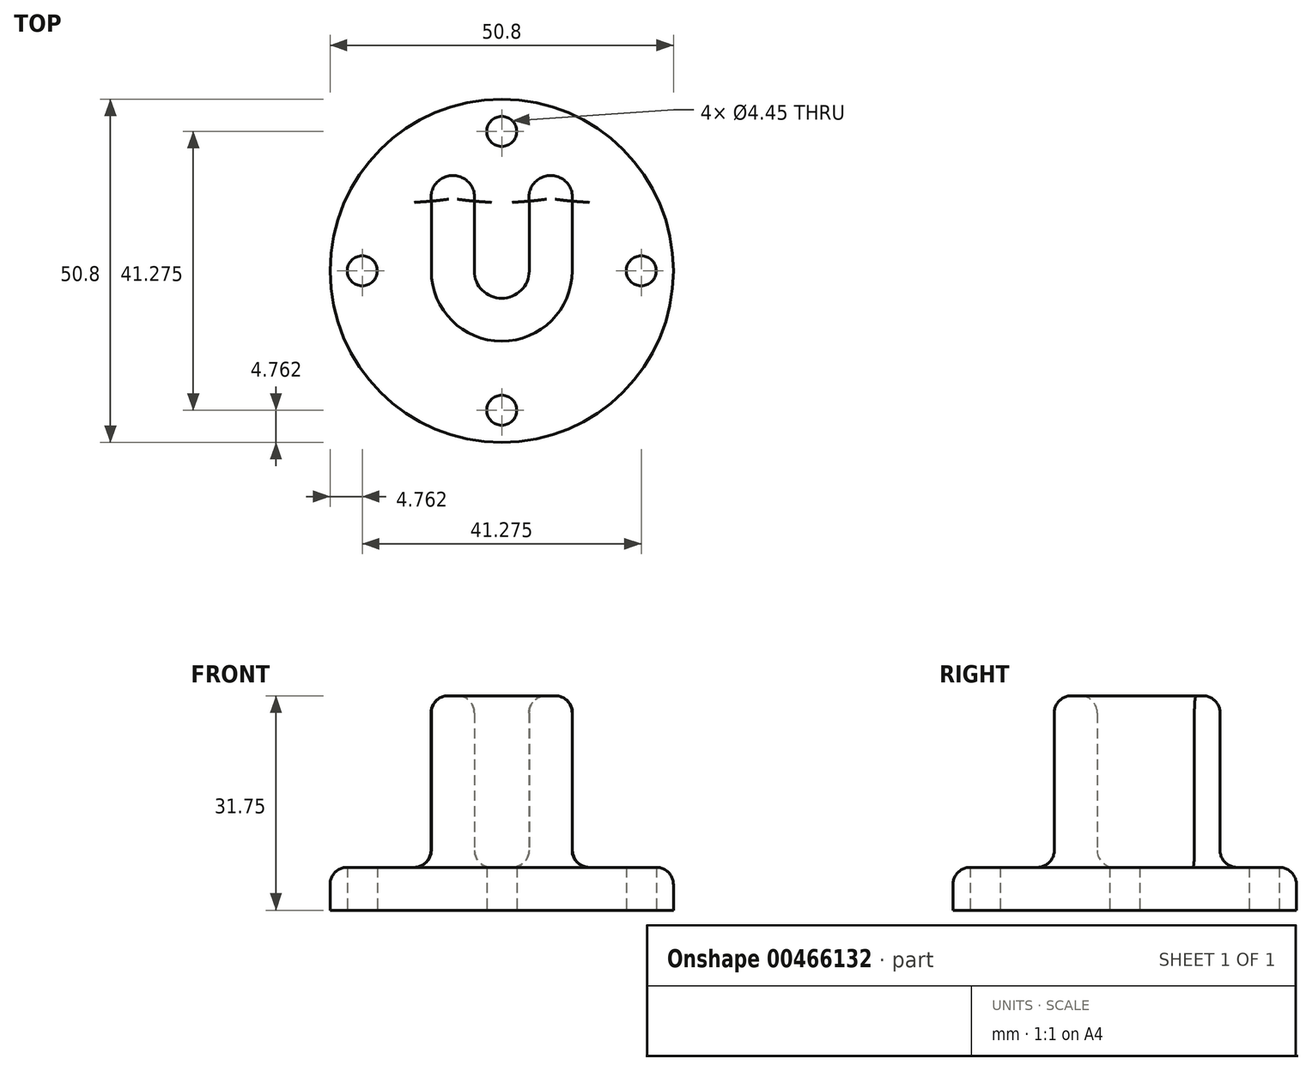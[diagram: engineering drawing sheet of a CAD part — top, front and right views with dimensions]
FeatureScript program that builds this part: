
annotation { "Feature Type Name" : "Feature", "Feature Type Description" : "" }
export const myFeature = defineFeature(function(context is Context, id is Id, definition is map)
    precondition{}
    {
        {
            var Q0;
            Q0=qCreatedBy(makeId("Top.planeOp"),FACE);
            var sketch = newSketch(context, id + "F0", { "sketchPlane" : qUnion([Q0])});
            skCircle(sketch, "E0", {"center": v(0, 0) * mm, "radius": 25.4 * mm});
            skLineSegment(sketch, "E1", {"start": v(0, 41.42) * mm, "end": v(0, -53.18) * mm, "construction": true});
            skLineSegment(sketch, "E2", {"start": v(45.55, 0) * mm, "end": v(-36.4, 0) * mm, "construction": true});
            skCircle(sketch, "E3", {"center": v(0, 0) * mm, "radius": 20.64 * mm, "construction": true});
            skCircle(sketch, "E4", {"center": v(0, 20.64) * mm, "radius": 2.22 * mm});
            skCircle(sketch, "E5.1.0", {"center": v(20.64, 0) * mm, "radius": 2.22 * mm});
            skCircle(sketch, "E5.2.0", {"center": v(0, -20.64) * mm, "radius": 2.22 * mm});
            skCircle(sketch, "E5.3.0", {"center": v(-20.64, 0) * mm, "radius": 2.22 * mm});
            skLineSegment(sketch, "E5.anchor1", {"start": v(0, 0) * mm, "end": v(0, 20.64) * mm, "construction": true});
            skLineSegment(sketch, "E5.anchor2", {"start": v(0, 0) * mm, "end": v(-20.64, 0) * mm, "construction": true});
            skArc(sketch, "E6", {"start": v(-4.06, 0) * mm, "mid": v(0, -4.06) * mm, "end": v(4.06, 0) * mm});
            skArc(sketch, "E7.0", {"start": v(1.4, 10.32) * mm, "mid": v(0.7, 10.4) * mm, "end": v(0, 10.41) * mm});
            skLineSegment(sketch, "E8", {"start": v(0, 10.32) * mm, "end": v(46.94, 10.32) * mm, "construction": true});
            skLineSegment(sketch, "E9", {"start": v(10.41, 0) * mm, "end": v(10.41, 10.32) * mm});
            skLineSegment(sketch, "E10", {"start": v(4.06, 0) * mm, "end": v(4.06, 10.32) * mm});
            skArc(sketch, "E11", {"start": v(10.41, 10.32) * mm, "mid": v(7.24, 14.11) * mm, "end": v(4.06, 10.32) * mm});
            skArc(sketch, "E12.trimOffspring", {"start": v(-10.41, 0) * mm, "mid": v(0, -10.41) * mm, "end": v(10.41, 0) * mm});
            skLineSegment(sketch, "E13.MirrorCS", {"start": v(-4.06, 0) * mm, "end": v(-4.06, 10.32) * mm});
            skArc(sketch, "E14.MirrorCS", {"start": v(-10.41, 10.32) * mm, "mid": v(-7.24, 14.11) * mm, "end": v(-4.06, 10.32) * mm});
            skLineSegment(sketch, "E15.MirrorCS", {"start": v(-10.41, 0) * mm, "end": v(-10.41, 10.32) * mm});
            skSolve(sketch);
        }
        {
            var Q0;
            Q0=makeQuery(id+"F0.imprint","IMPRINT",FACE,{"disambiguationData":[TD([[makeQuery(id+"F0.imprint","IMPRINT",EDGE,{"derivedFrom":sQuery(id+"F0.wireOp",EDGE,"E0")}),1.0]])]});
            var Q1;
            Q1=makeQuery(id+"F0.imprint","IMPRINT",FACE,{"disambiguationData":[TD([[makeQuery(id+"F0.imprint","IMPRINT",EDGE,{"derivedFrom":sQuery(id+"F0.wireOp",EDGE,"E6")}),-1.0]])]});
            var Q2;
            Q2=makeQuery(id+"F0.imprint","IMPRINT",FACE,{"disambiguationData":[TD([[makeQuery(id+"F0.imprint","IMPRINT",EDGE,{"derivedFrom":sQuery(id+"F0.wireOp",EDGE,"E5.2.0")}),1.0]])]});
            var Q3;
            Q3=makeQuery(id+"F0.imprint","IMPRINT",FACE,{"disambiguationData":[TD([[makeQuery(id+"F0.imprint","IMPRINT",EDGE,{"derivedFrom":sQuery(id+"F0.wireOp",EDGE,"E5.3.0")}),1.0]])]});
            var Q4;
            Q4=makeQuery(id+"F0.imprint","IMPRINT",FACE,{"disambiguationData":[TD([[makeQuery(id+"F0.imprint","IMPRINT",EDGE,{"derivedFrom":sQuery(id+"F0.wireOp",EDGE,"E4")}),1.0]])]});
            var Q5;
            Q5=makeQuery(id+"F0.imprint","IMPRINT",FACE,{"disambiguationData":[TD([[makeQuery(id+"F0.imprint","IMPRINT",EDGE,{"derivedFrom":sQuery(id+"F0.wireOp",EDGE,"E5.1.0")}),1.0]])]});
            extrude(context, id + "F1", {"entities" : qUnion([Q0, Q1, Q2, Q3, Q4, Q5]), "depth" : 6.35 * mm});
        }
        {
            var Q0;
            Q0=makeQuery(id+"F1.opExtrude","CAP_FACE",FACE,{"disambiguationData":[OSD([sQuery(id+"F0.wireOp",EDGE,"E0"),sQuery(id+"F0.wireOp",EDGE,"E4"),sQuery(id+"F0.wireOp",EDGE,"E5.1.0"),sQuery(id+"F0.wireOp",EDGE,"E5.2.0"),sQuery(id+"F0.wireOp",EDGE,"E5.3.0")])],"isStart":false});
            var sketch = newSketch(context, id + "F2", { "sketchPlane" : qUnion([Q0])});
            skLineSegment(sketch, "E16.0", {"start": v(-10.41, 0) * mm, "end": v(-10.41, 10.32) * mm});
            skArc(sketch, "E17.0", {"start": v(-10.41, 10.32) * mm, "mid": v(-7.24, 14.11) * mm, "end": v(-4.06, 10.32) * mm});
            skLineSegment(sketch, "E18.0", {"start": v(-4.06, 0) * mm, "end": v(-4.06, 10.32) * mm});
            skArc(sketch, "E19.0", {"start": v(-4.06, 0) * mm, "mid": v(0, -4.06) * mm, "end": v(4.06, 0) * mm});
            skArc(sketch, "E20.0", {"start": v(-10.41, 0) * mm, "mid": v(0, -10.41) * mm, "end": v(10.41, 0) * mm});
            skLineSegment(sketch, "E21.0", {"start": v(4.06, 0) * mm, "end": v(4.06, 10.32) * mm});
            skArc(sketch, "E22.0", {"start": v(10.41, 10.32) * mm, "mid": v(7.24, 14.11) * mm, "end": v(4.06, 10.32) * mm});
            skLineSegment(sketch, "E23.0", {"start": v(10.41, 0) * mm, "end": v(10.41, 10.32) * mm});
            skSolve(sketch);
        }
        {
            var Q0;
            Q0=makeQuery(id+"F2.imprint","IMPRINT",FACE,{"disambiguationData":[TD([[makeQuery(id+"F2.imprint","IMPRINT",EDGE,{"derivedFrom":sQuery(id+"F2.wireOp",EDGE,"E16.0")}),-1.0]])]});
            extrude(context, id + "F3", {"entities" : qUnion([Q0]), "operationType" : NewBodyOperationType.ADD, "depth" : 25.4 * mm});
        }
        {
            var Q0;
            Q0=makeQuery(id+"F1.opExtrude","CAP_EDGE",EDGE,{"disambiguationData":[OSD([sQuery(id+"F0.wireOp",EDGE,"E0")])],"isStart":false});
            fillet(context, id + "F4", {"entities" : qUnion([Q0]), "radius" : 2.54 * mm, "tangentPropagation" : true, "allowEdgeOverflow" : false});
        }
        {
            var Q0;
            Q0=makeQuery(id+"F3.opExtrude","CAP_FACE",FACE,{"disambiguationData":[OSD([sQuery(id+"F2.wireOp",EDGE,"E16.0"),sQuery(id+"F2.wireOp",EDGE,"E17.0"),sQuery(id+"F2.wireOp",EDGE,"E18.0"),sQuery(id+"F2.wireOp",EDGE,"E19.0"),sQuery(id+"F2.wireOp",EDGE,"E20.0"),sQuery(id+"F2.wireOp",EDGE,"E21.0"),sQuery(id+"F2.wireOp",EDGE,"E22.0"),sQuery(id+"F2.wireOp",EDGE,"E23.0")])],"isStart":false});
            var Q1;
            Q1=makeQuery(id+"F1.opExtrude","CAP_FACE",FACE,{"disambiguationData":[OSD([sQuery(id+"F0.wireOp",EDGE,"E0")])],"isStart":false});
            fillet(context, id + "F5", {"entities" : qUnion([Q0, Q1]), "radius" : 2.54 * mm, "tangentPropagation" : true, "allowEdgeOverflow" : false});
        }
        {
            var Q0;
            Q0=makeQuery(id+"F0.imprint","IMPRINT",FACE,{"disambiguationData":[TD([[makeQuery(id+"F0.imprint","IMPRINT",EDGE,{"derivedFrom":sQuery(id+"F0.wireOp",EDGE,"E5.1.0")}),1.0]])]});
            var Q1;
            Q1=makeQuery(id+"F0.imprint","IMPRINT",FACE,{"disambiguationData":[TD([[makeQuery(id+"F0.imprint","IMPRINT",EDGE,{"derivedFrom":sQuery(id+"F0.wireOp",EDGE,"E4")}),1.0]])]});
            var Q2;
            Q2=makeQuery(id+"F0.imprint","IMPRINT",FACE,{"disambiguationData":[TD([[makeQuery(id+"F0.imprint","IMPRINT",EDGE,{"derivedFrom":sQuery(id+"F0.wireOp",EDGE,"E5.3.0")}),1.0]])]});
            var Q3;
            Q3=makeQuery(id+"F0.imprint","IMPRINT",FACE,{"disambiguationData":[TD([[makeQuery(id+"F0.imprint","IMPRINT",EDGE,{"derivedFrom":sQuery(id+"F0.wireOp",EDGE,"E5.2.0")}),1.0]])]});
            extrude(context, id + "F6", {"entities" : qUnion([Q0, Q1, Q2, Q3]), "operationType" : NewBodyOperationType.REMOVE, "depth" : 25.4 * mm});
        }
    });
